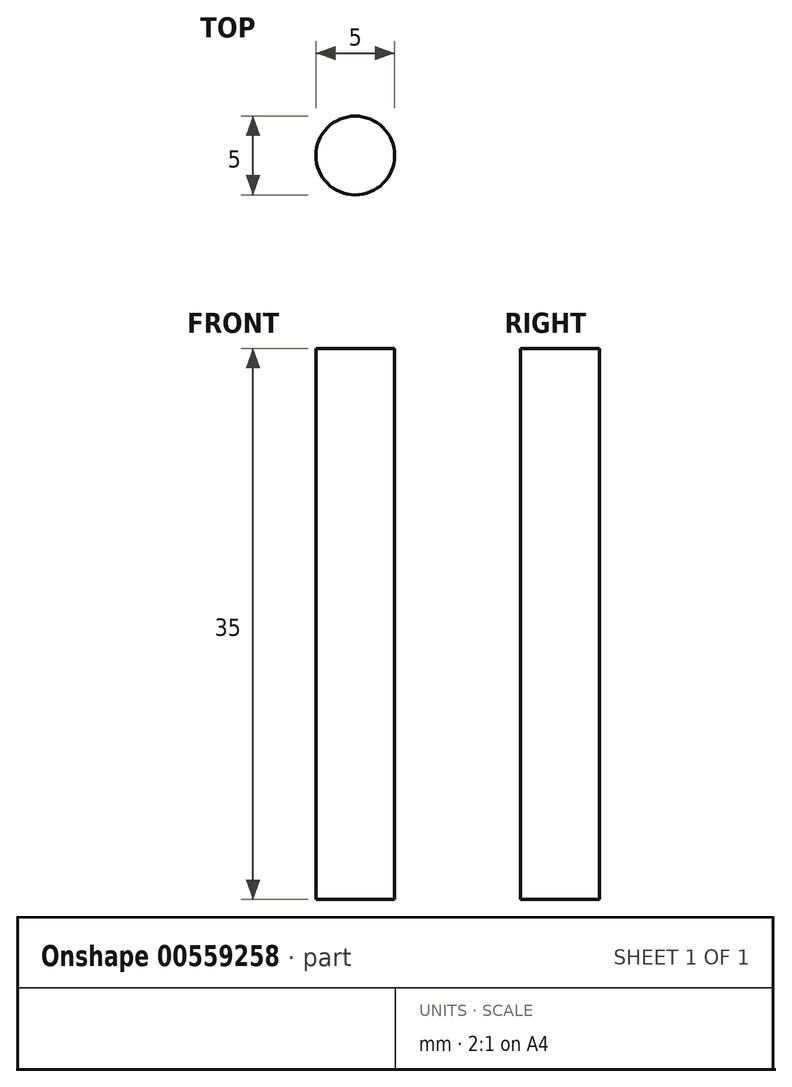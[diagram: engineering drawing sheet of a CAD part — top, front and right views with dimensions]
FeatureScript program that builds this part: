
annotation { "Feature Type Name" : "Feature", "Feature Type Description" : "" }
export const myFeature = defineFeature(function(context is Context, id is Id, definition is map)
    precondition{}
    {
        {
            var Q0;
            Q0=qCreatedBy(makeId("Top.planeOp"),FACE);
            var sketch = newSketch(context, id + "F0", { "sketchPlane" : qUnion([Q0])});
            skCircle(sketch, "E0", {"center": v(0, 0) * mm, "radius": 2.5 * mm});
            skSolve(sketch);
        }
        {
            var Q0;
            Q0=qSketchRegion(id+"F0",true);
            extrude(context, id + "F1", {"entities" : qUnion([Q0]), "endBound" : BoundingType.SYMMETRIC, "depth" : 35 * mm, "offsetDistance" : 25 * mm});
        }
    });
